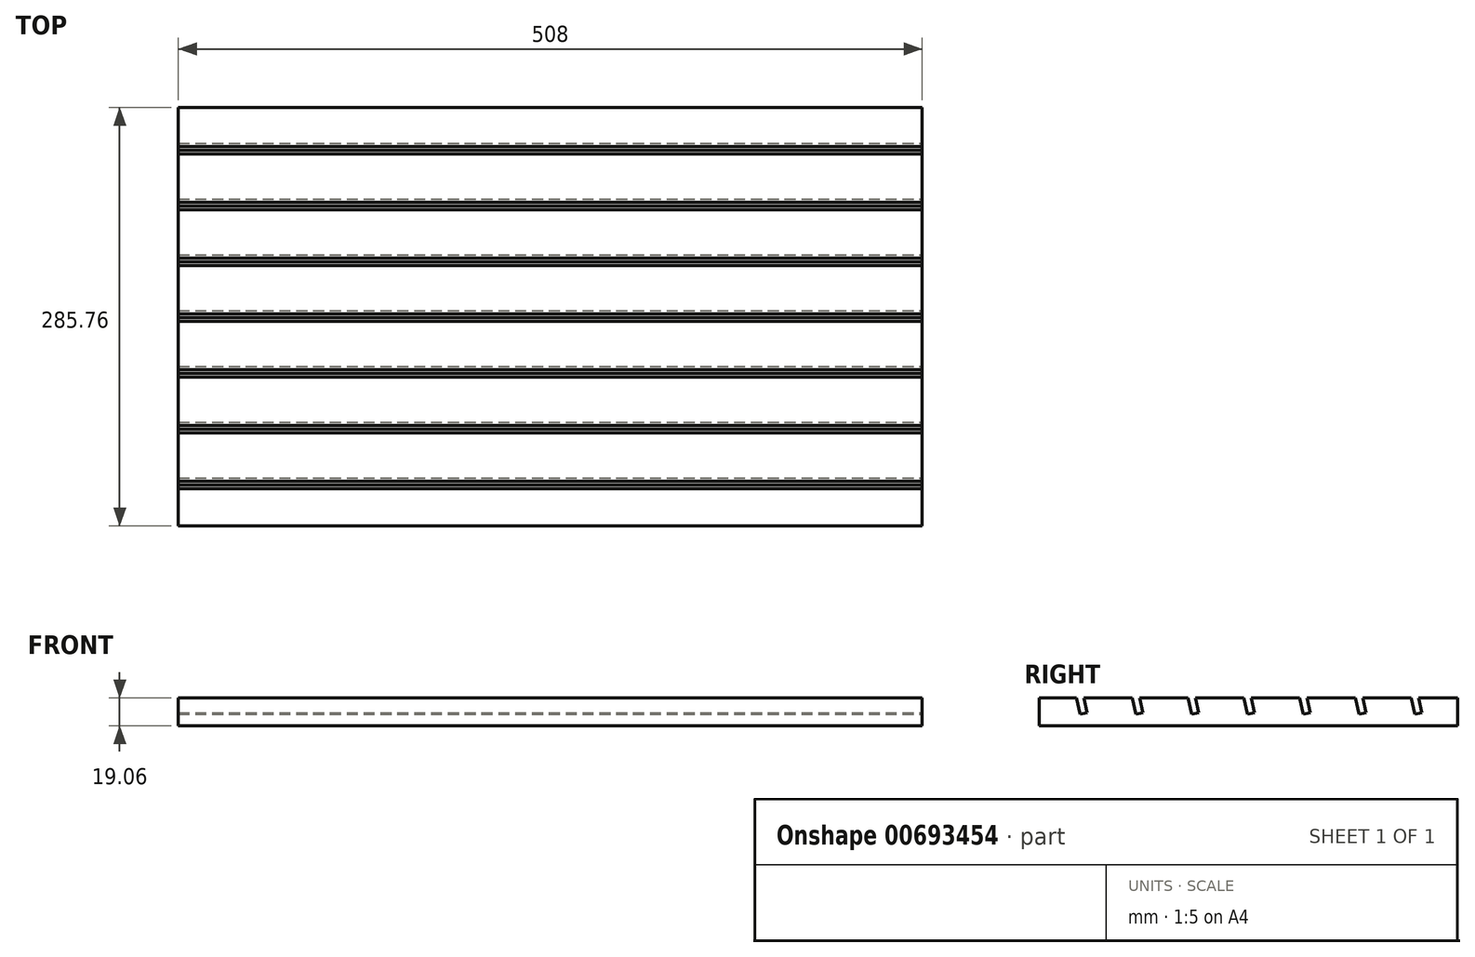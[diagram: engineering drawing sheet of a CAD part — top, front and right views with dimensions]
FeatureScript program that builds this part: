
annotation { "Feature Type Name" : "Feature", "Feature Type Description" : "" }
export const myFeature = defineFeature(function(context is Context, id is Id, definition is map)
    precondition{}
    {
        {
            var Q0;
            Q0=qCreatedBy(makeId("Right.planeOp"),FACE);
            var sketch = newSketch(context, id + "F0", { "sketchPlane" : qUnion([Q0])});
            skLineSegment(sketch, "E0.bottom", {"start": v(-142.87, 9.53) * mm, "end": v(142.88, 9.53) * mm});
            skLineSegment(sketch, "E0.top", {"start": v(-142.87, -9.53) * mm, "end": v(142.88, -9.53) * mm});
            skLineSegment(sketch, "E0.left", {"start": v(-142.87, 9.53) * mm, "end": v(-142.87, -9.52) * mm});
            skLineSegment(sketch, "E0.right", {"start": v(142.88, 9.53) * mm, "end": v(142.88, -9.52) * mm});
            skPoint(sketch, "E0.middle", {"position": v(0, 0) * mm});
            skSolve(sketch);
        }
        {
            var Q0;
            Q0=makeQuery(id+"F0.imprint","IMPRINT",FACE,{"disambiguationData":[TD([[makeQuery(id+"F0.imprint","IMPRINT",EDGE,{"derivedFrom":sQuery(id+"F0.wireOp",EDGE,"E0.bottom")}),-1.0]])]});
            extrude(context, id + "F1", {"entities" : qUnion([Q0]), "depth" : 254 * mm, "offsetDistance" : 25.4 * mm, "hasSecondDirection" : true, "secondDirectionOppositeDirection" : true, "secondDirectionDepth" : 254 * mm});
        }
        {
            var Q0;
            Q0=makeQuery(id+"F1.opExtrude","CAP_FACE",FACE,{"disambiguationData":[OSD([sQuery(id+"F0.wireOp",EDGE,"E0.bottom"),sQuery(id+"F0.wireOp",EDGE,"E0.top"),sQuery(id+"F0.wireOp",EDGE,"E0.left"),sQuery(id+"F0.wireOp",EDGE,"E0.right")])],"isStart":false});
            var sketch = newSketch(context, id + "F2", { "sketchPlane" : qUnion([Q0])});
            skLineSegment(sketch, "E1.bottom", {"start": v(-117.47, 9.53) * mm, "end": v(-112.66, 10.55) * mm});
            skLineSegment(sketch, "E1.top", {"start": v(-115.09, -1.7) * mm, "end": v(-110.28, -0.68) * mm});
            skLineSegment(sketch, "E1.left", {"start": v(-117.47, 9.53) * mm, "end": v(-115.09, -1.7) * mm});
            skLineSegment(sketch, "E1.right", {"start": v(-112.66, 10.55) * mm, "end": v(-110.28, -0.68) * mm});
            skLineSegment(sketch, "E2.bottom", {"start": v(-79.37, 9.53) * mm, "end": v(-74.56, 10.55) * mm});
            skLineSegment(sketch, "E2.top", {"start": v(-76.99, -1.7) * mm, "end": v(-72.18, -0.68) * mm});
            skLineSegment(sketch, "E2.left", {"start": v(-79.37, 9.53) * mm, "end": v(-76.99, -1.7) * mm});
            skLineSegment(sketch, "E2.right", {"start": v(-74.56, 10.55) * mm, "end": v(-72.18, -0.68) * mm});
            skLineSegment(sketch, "E3.bottom", {"start": v(-41.27, 9.53) * mm, "end": v(-36.46, 10.55) * mm});
            skLineSegment(sketch, "E3.top", {"start": v(-38.89, -1.7) * mm, "end": v(-34.08, -0.68) * mm});
            skLineSegment(sketch, "E3.left", {"start": v(-41.27, 9.53) * mm, "end": v(-38.89, -1.7) * mm});
            skLineSegment(sketch, "E3.right", {"start": v(-36.46, 10.55) * mm, "end": v(-34.08, -0.68) * mm});
            skLineSegment(sketch, "E4.bottom", {"start": v(-3.17, 9.53) * mm, "end": v(1.64, 10.55) * mm});
            skLineSegment(sketch, "E4.top", {"start": v(-0.79, -1.7) * mm, "end": v(4.02, -0.68) * mm});
            skLineSegment(sketch, "E4.left", {"start": v(-3.17, 9.53) * mm, "end": v(-0.79, -1.7) * mm});
            skLineSegment(sketch, "E4.right", {"start": v(1.64, 10.55) * mm, "end": v(4.02, -0.68) * mm});
            skLineSegment(sketch, "E5.bottom", {"start": v(34.93, 9.53) * mm, "end": v(39.74, 10.55) * mm});
            skLineSegment(sketch, "E5.top", {"start": v(37.31, -1.7) * mm, "end": v(42.12, -0.68) * mm});
            skLineSegment(sketch, "E5.left", {"start": v(34.93, 9.53) * mm, "end": v(37.31, -1.7) * mm});
            skLineSegment(sketch, "E5.right", {"start": v(39.74, 10.55) * mm, "end": v(42.12, -0.68) * mm});
            skLineSegment(sketch, "E6.bottom", {"start": v(73.03, 9.53) * mm, "end": v(77.84, 10.55) * mm});
            skLineSegment(sketch, "E6.top", {"start": v(75.41, -1.7) * mm, "end": v(80.22, -0.68) * mm});
            skLineSegment(sketch, "E6.left", {"start": v(73.03, 9.53) * mm, "end": v(75.41, -1.7) * mm});
            skLineSegment(sketch, "E6.right", {"start": v(77.84, 10.55) * mm, "end": v(80.22, -0.68) * mm});
            skLineSegment(sketch, "E7.bottom", {"start": v(111.13, 9.53) * mm, "end": v(115.94, 10.55) * mm});
            skLineSegment(sketch, "E7.top", {"start": v(113.51, -1.7) * mm, "end": v(118.32, -0.68) * mm});
            skLineSegment(sketch, "E7.left", {"start": v(111.13, 9.53) * mm, "end": v(113.51, -1.7) * mm});
            skLineSegment(sketch, "E7.right", {"start": v(115.94, 10.55) * mm, "end": v(118.32, -0.68) * mm});
            skSolve(sketch);
        }
        {
            var Q0;
            {var subQ0=sQuery(id+"F2.wireOp",EDGE,"E1.top");Q0=makeQuery(id+"F2.imprint","IMPRINT",FACE,{"disambiguationData":[TD([[makeQuery(id+"F2.imprint","IMPRINT",EDGE,{"derivedFrom":subQ0}),1.0]])]});}
            var Q1;
            {var subQ0=sQuery(id+"F2.wireOp",EDGE,"E2.top");Q1=makeQuery(id+"F2.imprint","IMPRINT",FACE,{"disambiguationData":[TD([[makeQuery(id+"F2.imprint","IMPRINT",EDGE,{"derivedFrom":subQ0}),1.0]])]});}
            var Q2;
            {var subQ0=sQuery(id+"F2.wireOp",EDGE,"E3.top");Q2=makeQuery(id+"F2.imprint","IMPRINT",FACE,{"disambiguationData":[TD([[makeQuery(id+"F2.imprint","IMPRINT",EDGE,{"derivedFrom":subQ0}),1.0]])]});}
            var Q3;
            {var subQ0=sQuery(id+"F2.wireOp",EDGE,"E4.top");Q3=makeQuery(id+"F2.imprint","IMPRINT",FACE,{"disambiguationData":[TD([[makeQuery(id+"F2.imprint","IMPRINT",EDGE,{"derivedFrom":subQ0}),1.0]])]});}
            var Q4;
            {var subQ0=sQuery(id+"F2.wireOp",EDGE,"E5.top");Q4=makeQuery(id+"F2.imprint","IMPRINT",FACE,{"disambiguationData":[TD([[makeQuery(id+"F2.imprint","IMPRINT",EDGE,{"derivedFrom":subQ0}),1.0]])]});}
            var Q5;
            {var subQ0=sQuery(id+"F2.wireOp",EDGE,"E6.top");Q5=makeQuery(id+"F2.imprint","IMPRINT",FACE,{"disambiguationData":[TD([[makeQuery(id+"F2.imprint","IMPRINT",EDGE,{"derivedFrom":subQ0}),1.0]])]});}
            var Q6;
            {var subQ0=sQuery(id+"F2.wireOp",EDGE,"E7.top");Q6=makeQuery(id+"F2.imprint","IMPRINT",FACE,{"disambiguationData":[TD([[makeQuery(id+"F2.imprint","IMPRINT",EDGE,{"derivedFrom":subQ0}),1.0]])]});}
            extrude(context, id + "F3", {"entities" : qUnion([Q0, Q1, Q2, Q3, Q4, Q5, Q6]), "operationType" : NewBodyOperationType.REMOVE, "endBound" : BoundingType.THROUGH_ALL, "oppositeDirection" : true, "depth" : 25.4 * mm, "offsetDistance" : 25.4 * mm});
        }
    });
